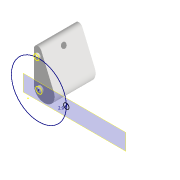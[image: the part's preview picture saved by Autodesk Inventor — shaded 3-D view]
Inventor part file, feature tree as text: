
AUTODESK INVENTOR PART (.ipt)
format: ipt  version: 2022 (Build 260153000, 153)  size: 130,560 bytes
history: native  units: mm
features: sketch x5, extrude x4, other x3, projected_geometry x2, fillet x1, plane x1, reference x1
ambient origin geometry x8: Origin, YZ Plane, XZ Plane, XY Plane, X Axis, Y Axis, Z Axis, Center Point
bodies: Volumenkörper1 (feature_tree)
feature tree (17):
  extrude  "Extrusion1"  Depth=2.0mm
  fillet  "Rundung1"  Radius=2.0mm
  extrude  "Extrusion2"  Depth=22.0mm TaperAngle=0.0deg
  extrude  "Extrusion3"  Depth=2.0mm
  plane  "Arbeitsebene1"
  sketch  "Skizze4"  dims[d8=2.9mm d9=4.0mm d10=0.0mm]
  extrude  "Extrusion4"  Depth=4.0mm TaperAngle=0.0deg
  sketch  "Skizze1"  dims[d0=20.0mm d1=3.0mm d2=2.0mm]
  reference  "Referenz1"
  sketch  "Skizze2"  dims[d3=2.0mm d4=22.0mm d5=0.0mm]
  projected_geometry  "Projizierte Kontur1"
  sketch  "Skizze3"  dims[d6=0.2mm d7=2.0mm]
  sketch  "Skizze5"  dims[d11=4.0mm d12=0.0mm d13=2.9mm d14=11.0mm d15=2.8mm d16=10.0mm d17=0.0mm]
  projected_geometry  "Projizierte Kontur2"
  other  "Anglerfish.iam"
  other  "Anglerfish_coverslipclamp_top:1"
  other  "Anglerfish_lunchbox_m12large_flipped_v0.iam"
